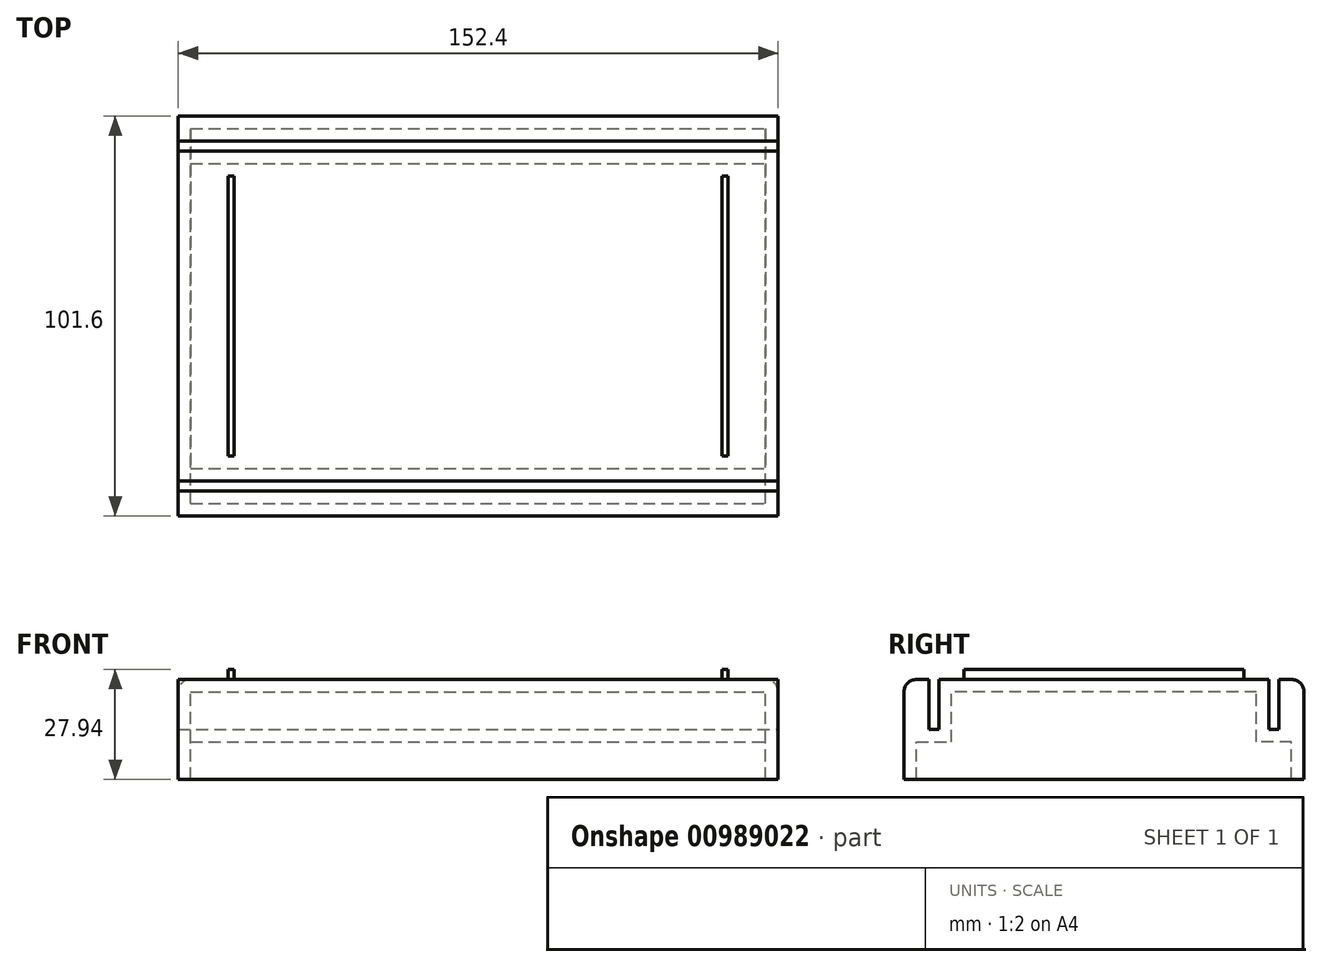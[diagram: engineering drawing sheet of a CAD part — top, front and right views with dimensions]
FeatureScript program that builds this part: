
annotation { "Feature Type Name" : "Feature", "Feature Type Description" : "" }
export const myFeature = defineFeature(function(context is Context, id is Id, definition is map)
    precondition{}
    {
        {
            var Q0;
            Q0=qCreatedBy(makeId("Right.planeOp"),FACE);
            var sketch = newSketch(context, id + "F0", { "sketchPlane" : qUnion([Q0])});
            skLineSegment(sketch, "E0.bottom", {"start": v(0, 0) * mm, "end": v(101.6, 0) * mm});
            skLineSegment(sketch, "E0.top", {"start": v(0, 25.4) * mm, "end": v(101.6, 25.4) * mm});
            skLineSegment(sketch, "E0.left", {"start": v(0, 0) * mm, "end": v(0, 25.4) * mm});
            skLineSegment(sketch, "E0.right", {"start": v(101.6, 0) * mm, "end": v(101.6, 25.4) * mm});
            skSolve(sketch);
        }
        {
            var Q0;
            Q0 = qSketchRegion(id + "F0", true);
            extrude(context, id + "F1", {"entities" : qUnion([Q0]), "oppositeDirection" : true, "depth" : 152.4 * mm, "offsetDistance" : 25.4 * mm});
        }
        {
            var Q0;
            Q0=makeQuery(id+"F1.opExtrude","CAP_FACE",FACE,{"disambiguationData":[OSD([sQuery(id+"F0.wireOp",EDGE,"E0.bottom"),sQuery(id+"F0.wireOp",EDGE,"E0.top"),sQuery(id+"F0.wireOp",EDGE,"E0.left"),sQuery(id+"F0.wireOp",EDGE,"E0.right")])],"isStart":true});
            var sketch = newSketch(context, id + "F2", { "sketchPlane" : qUnion([Q0])});
            skLineSegment(sketch, "E1", {"start": v(6.35, 25.4) * mm, "end": v(6.35, 12.7) * mm});
            skLineSegment(sketch, "E2", {"start": v(6.35, 12.7) * mm, "end": v(8.9, 12.7) * mm});
            skLineSegment(sketch, "E3", {"start": v(8.9, 12.7) * mm, "end": v(8.9, 25.4) * mm});
            skLineSegment(sketch, "E4", {"start": v(50.8, 25.4) * mm, "end": v(50.8, 0) * mm});
            skLineSegment(sketch, "E5.MirrorCS", {"start": v(95.25, 25.4) * mm, "end": v(95.25, 12.7) * mm});
            skLineSegment(sketch, "E6.MirrorCS", {"start": v(95.25, 12.7) * mm, "end": v(92.71, 12.7) * mm});
            skLineSegment(sketch, "E7.MirrorCS", {"start": v(92.71, 12.7) * mm, "end": v(92.71, 25.4) * mm});
            skSolve(sketch);
        }
        {
            var Q0;
            Q0 = qSketchRegion(id + "F2", true);
            var Q1;
            {var subQ0=sQuery(id+"F2.wireOp",EDGE,"E1");Q1=makeQuery(id+"F2.imprint","IMPRINT",FACE,{"disambiguationData":[TD([[makeQuery(id+"F2.imprint","IMPRINT",EDGE,{"derivedFrom":subQ0}),1.0]])]});}
            var Q2;
            {var subQ0=sQuery(id+"F2.wireOp",EDGE,"E5.MirrorCS");Q2=makeQuery(id+"F2.imprint","IMPRINT",FACE,{"disambiguationData":[TD([[makeQuery(id+"F2.imprint","IMPRINT",EDGE,{"derivedFrom":subQ0}),-1.0]])]});}
            extrude(context, id + "F3", {"entities" : qUnion([Q0, Q1, Q2]), "operationType" : NewBodyOperationType.REMOVE, "endBound" : BoundingType.THROUGH_ALL, "oppositeDirection" : true, "depth" : 25.4 * mm, "offsetDistance" : 25.4 * mm});
        }
        {
            var Q0;
            {var subQ2=sQuery(id+"F0.wireOp",EDGE,"E0.top");Q0=makeQuery(id+"F3.boolean.opBoolean","SPLIT",FACE,{"disambiguationData":[TD([makeQuery(id+"F3.opExtrude","SWEPT_FACE",FACE,{"disambiguationData":[OSD([sQuery(id+"F2.wireOp",EDGE,"E3")])]})])],"derivedFrom":makeQuery(id+"F1.opExtrude","SWEPT_FACE",FACE,{"disambiguationData":[OSD([subQ2])]})});}
            var sketch = newSketch(context, id + "F4", { "sketchPlane" : qUnion([Q0])});
            skLineSegment(sketch, "E8.bottom", {"start": v(-139.7, 86.36) * mm, "end": v(-138.18, 86.36) * mm});
            skLineSegment(sketch, "E8.top", {"start": v(-139.7, 15.24) * mm, "end": v(-138.18, 15.24) * mm});
            skLineSegment(sketch, "E8.left", {"start": v(-139.7, 86.36) * mm, "end": v(-139.7, 15.24) * mm});
            skLineSegment(sketch, "E8.right", {"start": v(-138.18, 86.36) * mm, "end": v(-138.18, 15.24) * mm});
            skLineSegment(sketch, "E9", {"start": v(-76.2, 92.71) * mm, "end": v(-76.2, 8.9) * mm});
            skLineSegment(sketch, "E10.MirrorCS", {"start": v(-12.7, 86.36) * mm, "end": v(-12.7, 15.24) * mm});
            skLineSegment(sketch, "E11.MirrorCS", {"start": v(-14.22, 86.36) * mm, "end": v(-14.22, 15.24) * mm});
            skLineSegment(sketch, "E12.MirrorCS", {"start": v(-12.7, 86.36) * mm, "end": v(-14.22, 86.36) * mm});
            skLineSegment(sketch, "E13.MirrorCS", {"start": v(-12.7, 15.24) * mm, "end": v(-14.22, 15.24) * mm});
            skSolve(sketch);
        }
        {
            var Q0;
            Q0 = qSketchRegion(id + "F4", true);
            extrude(context, id + "F5", {"entities" : qUnion([Q0]), "operationType" : NewBodyOperationType.ADD, "depth" : 2.54 * mm, "offsetDistance" : 25.4 * mm});
        }
        {
            var Q0;
            Q0=makeQuery(id+"F1.opExtrude","SWEPT_EDGE",EDGE,{"disambiguationData":[OSD([sQuery(id+"F0.wireOp",EDGE,"E0.top"),sQuery(id+"F0.wireOp",EDGE,"E0.left")])]});
            var Q1;
            Q1=makeQuery(id+"F1.opExtrude","SWEPT_EDGE",EDGE,{"disambiguationData":[OSD([sQuery(id+"F0.wireOp",EDGE,"E0.top"),sQuery(id+"F0.wireOp",EDGE,"E0.right")])]});
            var Q2;
            {var subQ0=sQuery(id+"F0.wireOp",EDGE,"E0.top");Q2=makeQuery(id+"F3.boolean.opBoolean","SPLIT",EDGE,{"disambiguationData":[TD([makeQuery(id+"F3.opExtrude","SWEPT_FACE",FACE,{"disambiguationData":[OSD([sQuery(id+"F2.wireOp",EDGE,"E3")])]})])],"derivedFrom":makeQuery(id+"F1.opExtrude","CAP_EDGE",EDGE,{"disambiguationData":[OSD([subQ0])],"isStart":true})});}
            var Q3;
            {var subQ0=sQuery(id+"F0.wireOp",EDGE,"E0.top");Q3=makeQuery(id+"F3.boolean.opBoolean","SPLIT",EDGE,{"disambiguationData":[TD([makeQuery(id+"F3.opExtrude","SWEPT_FACE",FACE,{"disambiguationData":[OSD([sQuery(id+"F2.wireOp",EDGE,"E3")])]})])],"derivedFrom":makeQuery(id+"F1.opExtrude","CAP_EDGE",EDGE,{"disambiguationData":[OSD([subQ0])],"isStart":false})});}
            fillet(context, id + "F6", {"entities" : qUnion([Q0, Q1, Q2, Q3]), "radius" : 3.17 * mm, "tangentPropagation" : true, "allowEdgeOverflow" : false});
        }
        {
            var Q0;
            Q0=makeQuery(id+"F1.opExtrude","SWEPT_FACE",FACE,{"disambiguationData":[OSD([sQuery(id+"F0.wireOp",EDGE,"E0.bottom")])]});
            shell(context, id + "F7", {"entities" : qUnion([Q0]), "thickness" : 3.17 * mm});
        }
    });
